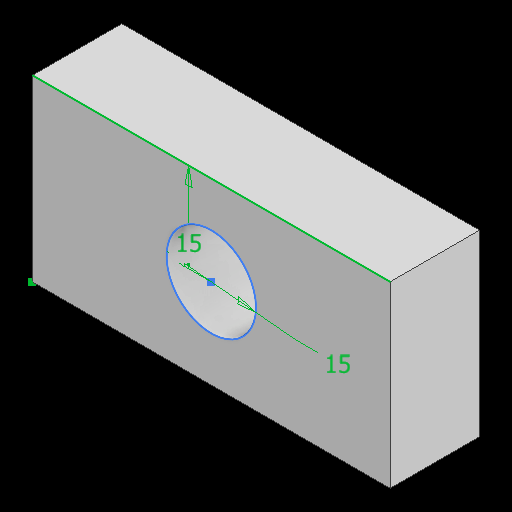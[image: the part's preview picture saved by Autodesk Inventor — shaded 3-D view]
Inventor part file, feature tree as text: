
AUTODESK INVENTOR PART (.ipt)
format: ipt  version: 2025.1 (Build 291241000, 241)  size: 101,888 bytes
history: native  units: in
note: dims shown in document units (in); Inventor stores cm internally (conversion verified against a paired STEP export)
features: sketch x3, extrude x2, other x1
ambient origin geometry x8: Origin, YZ Plane, XZ Plane, XY Plane, X Axis, Y Axis, Z Axis, Center Point
bodies: Body1 (feature_tree)
feature tree (6):
  other  "솔리드1"
  extrude  "돌출1"  Depth=2.3622in
  sketch  "스케치2"
  extrude  "돌출2"  Depth=1.1811in
  sketch  "스케치1"
  sketch  "스케치3"
